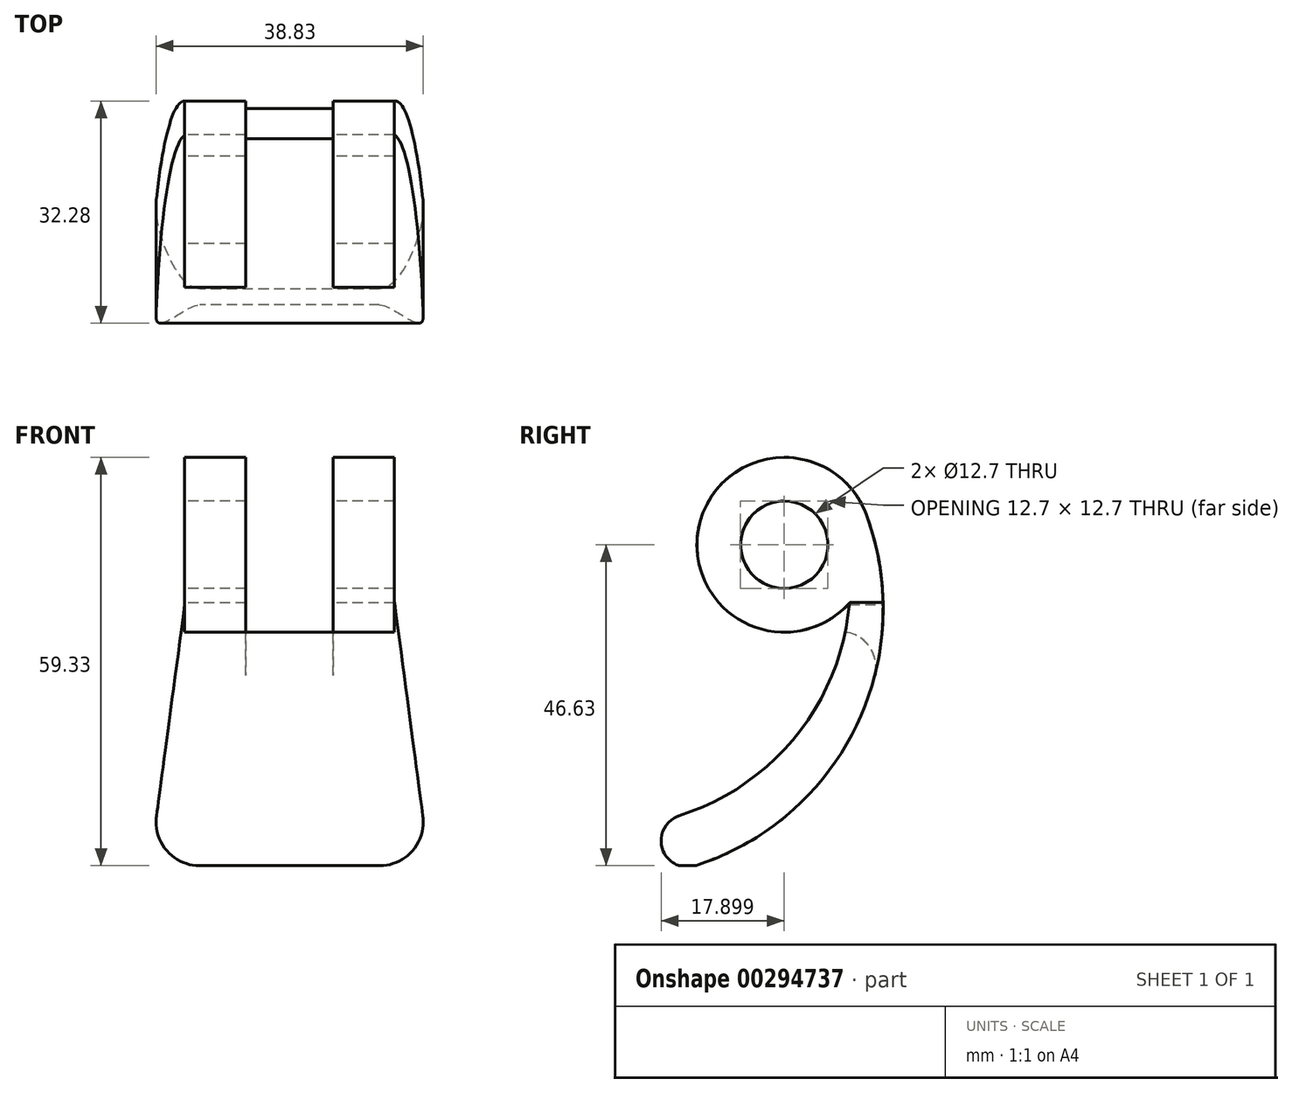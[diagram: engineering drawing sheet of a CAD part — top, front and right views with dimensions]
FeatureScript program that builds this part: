
annotation { "Feature Type Name" : "Feature", "Feature Type Description" : "" }
export const myFeature = defineFeature(function(context is Context, id is Id, definition is map)
    precondition{}
    {
        {
            var Q0;
            Q0=qCreatedBy(makeId("Front.planeOp"),FACE);
            var sketch = newSketch(context, id + "F0", { "sketchPlane" : qUnion([Q0])});
            skCircle(sketch, "E0", {"center": v(0, 0) * mm, "radius": 12.7 * mm});
            skCircle(sketch, "E1", {"center": v(0, 0) * mm, "radius": 6.35 * mm});
            skSolve(sketch);
        }
        {
            var Q0;
            Q0=qSketchRegion(id+"F0",true);
            extrude(context, id + "F1", {"entities" : qUnion([Q0]), "endBound" : BoundingType.SYMMETRIC, "depth" : 30.48 * mm});
        }
        {
            var Q0;
            Q0=qCreatedBy(makeId("Front.planeOp"),FACE);
            var sketch = newSketch(context, id + "F2", { "sketchPlane" : qUnion([Q0])});
            skArc(sketch, "E2", {"start": v(-12.94, -46.63) * mm, "mid": v(10.43, -26.42) * mm, "end": v(11.9, 4.44) * mm});
            skArc(sketch, "E3", {"start": v(-15.24, -39.37) * mm, "mid": v(1.83, -27.66) * mm, "end": v(9.5, -8.43) * mm});
            skArc(sketch, "E4", {"start": v(-15.24, -39.37) * mm, "mid": v(-17.73, -44.15) * mm, "end": v(-12.94, -46.63) * mm});
            skArc(sketch, "E5", {"start": v(9.5, -8.43) * mm, "mid": v(12.48, -2.33) * mm, "end": v(11.9, 4.44) * mm});
            skSolve(sketch);
        }
        {
            var Q0;
            Q0=qSketchRegion(id+"F2",true);
            extrude(context, id + "F3", {"entities" : qUnion([Q0]), "operationType" : NewBodyOperationType.ADD, "endBound" : BoundingType.SYMMETRIC, "depth" : 40.64 * mm});
        }
        {
            var Q0;
            Q0=qCreatedBy(makeId("Front.planeOp"),FACE);
            var sketch = newSketch(context, id + "F4", { "sketchPlane" : qUnion([Q0])});
            skCircle(sketch, "E6", {"center": v(0, 0) * mm, "radius": 12.7 * mm});
            skSolve(sketch);
        }
        {
            var Q0;
            Q0=qSketchRegion(id+"F4",true);
            extrude(context, id + "F5", {"entities" : qUnion([Q0]), "operationType" : NewBodyOperationType.REMOVE, "endBound" : BoundingType.SYMMETRIC, "depth" : 12.7 * mm});
        }
        {
            var Q0;
            Q0=qCreatedBy(makeId("Right.planeOp"),FACE);
            var sketch = newSketch(context, id + "F6", { "sketchPlane" : qUnion([Q0])});
            skLineSegment(sketch, "E7.bottom", {"start": v(-6.35, 12.7) * mm, "end": v(6.35, 12.7) * mm});
            skLineSegment(sketch, "E7.top", {"start": v(-6.35, -12.7) * mm, "end": v(6.35, -12.7) * mm});
            skLineSegment(sketch, "E7.left", {"start": v(-6.35, 12.7) * mm, "end": v(-6.35, -12.7) * mm});
            skLineSegment(sketch, "E7.right", {"start": v(6.35, 12.7) * mm, "end": v(6.35, -12.7) * mm});
            skSolve(sketch);
        }
        {
            var Q0;
            Q0=qSketchRegion(id+"F6",true);
            extrude(context, id + "F7", {"entities" : qUnion([Q0]), "operationType" : NewBodyOperationType.REMOVE, "endBound" : BoundingType.THROUGH_ALL, "depth" : 25.4 * mm});
        }
        {
            var Q0;
            Q0=makeQuery(id+"F7.boolean.opBoolean","INTERSECT",EDGE,{"derivedFrom":[makeQuery(id+"F3.opExtrude","SWEPT_FACE",FACE,{"disambiguationData":[OSD([sQuery(id+"F2.wireOp",EDGE,"E2")])]}),makeQuery(id+"F7.opExtrude","SWEPT_FACE",FACE,{"disambiguationData":[OSD([sQuery(id+"F6.wireOp",EDGE,"E7.top")])]})]});
            fillet(context, id + "F8", {"entities" : qUnion([Q0]), "radius" : 5.08 * mm, "tangentPropagation" : true, "allowEdgeOverflow" : false});
        }
        {
            var Q0;
            Q0=qCreatedBy(makeId("Right.planeOp"),FACE);
            var sketch = newSketch(context, id + "F9", { "sketchPlane" : qUnion([Q0])});
            skLineSegment(sketch, "E8", {"start": v(0, 0) * mm, "end": v(0, 34.87) * mm, "construction": true});
            skSolve(sketch);
        }
        {
            var Q0;
            Q0=makeQuery(id+"F1.opExtrude","SWEPT_BODY",BODY,{"disambiguationData":[OSD([sQuery(id+"F0.wireOp",EDGE,"E0"),sQuery(id+"F0.wireOp",EDGE,"E1")])]});
            var Q1;
            Q1=sQuery(id+"F9.wireOp",EDGE,"E8");
            transform(context, id + "F10", {"entities" : qUnion([Q0]), "transformType" : TransformType.ROTATION, "transformAxis" : qUnion([Q1]), "angle" : 1.57 * radian, "makeCopy" : false});
        }
        {
            var Q0;
            Q0=qCreatedBy(makeId("Front.planeOp"),FACE);
            var sketch = newSketch(context, id + "F11", { "sketchPlane" : qUnion([Q0])});
            skLineSegment(sketch, "E9", {"start": v(15.24, -8.38) * mm, "end": v(19.37, -39.45) * mm});
            skLineSegment(sketch, "E10", {"start": v(13.07, -46.63) * mm, "end": v(-13.06, -46.63) * mm});
            skLineSegment(sketch, "E11", {"start": v(-19.36, -39.44) * mm, "end": v(-15.24, -8.7) * mm});
            skLineSegment(sketch, "E12", {"start": v(-15.24, -8.7) * mm, "end": v(-15.24, 12.7) * mm});
            skLineSegment(sketch, "E13", {"start": v(-15.24, 12.7) * mm, "end": v(15.24, 12.7) * mm});
            skLineSegment(sketch, "E14", {"start": v(15.24, 12.7) * mm, "end": v(15.24, -8.38) * mm});
            skPoint(sketch, "E15.visualSharp", {"position": v(20.32, -46.63) * mm});
            skArc(sketch, "E15.filletArc", {"start": v(13.07, -46.63) * mm, "mid": v(17.85, -44.47) * mm, "end": v(19.37, -39.45) * mm});
            skPoint(sketch, "E16.visualSharp", {"position": v(-20.32, -46.63) * mm});
            skArc(sketch, "E16.filletArc", {"start": v(-19.36, -39.44) * mm, "mid": v(-17.84, -44.47) * mm, "end": v(-13.06, -46.63) * mm});
            skSolve(sketch);
        }
        {
            var Q0;
            Q0=qSketchRegion(id+"F11",true);
            extrude(context, id + "F12", {"entities" : qUnion([Q0]), "operationType" : NewBodyOperationType.INTERSECT, "endBound" : BoundingType.SYMMETRIC, "depth" : 76.2 * mm});
        }
    });
